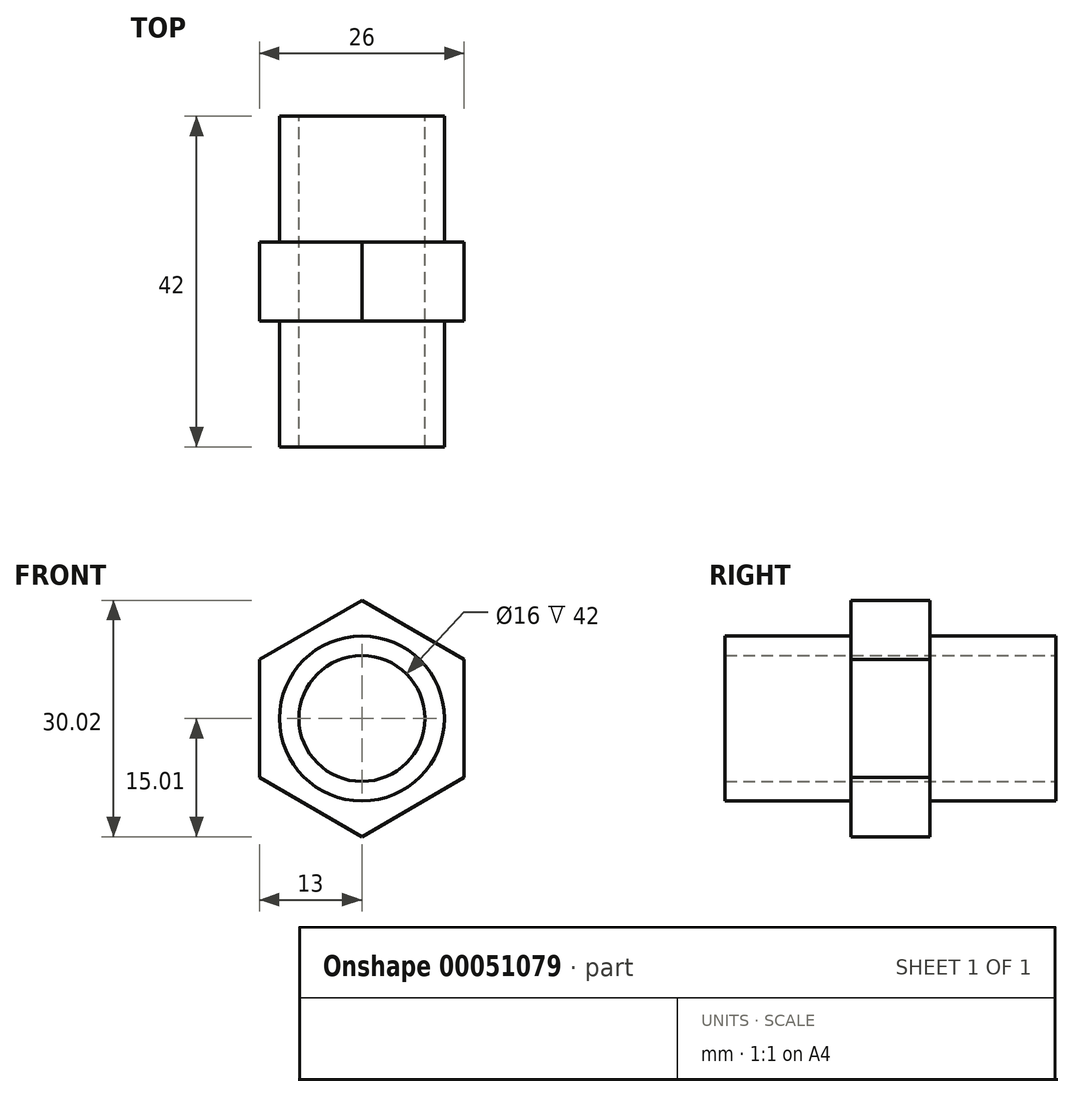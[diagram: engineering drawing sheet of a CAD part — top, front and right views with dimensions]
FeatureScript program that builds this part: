
annotation { "Feature Type Name" : "Feature", "Feature Type Description" : "" }
export const myFeature = defineFeature(function(context is Context, id is Id, definition is map)
    precondition{}
    {
        {
            var Q0;
            Q0=qCreatedBy(makeId("Front.planeOp"),FACE);
            var sketch = newSketch(context, id + "F0", { "sketchPlane" : qUnion([Q0])});
            skCircle(sketch, "E0", {"center": v(0, 0) * mm, "radius": 10.48 * mm});
            skCircle(sketch, "E1", {"center": v(0, 0) * mm, "radius": 8 * mm});
            skSolve(sketch);
        }
        {
            var Q0;
            Q0=qSketchRegion(id+"F0",true);
            extrude(context, id + "F1", {"entities" : qUnion([Q0]), "depth" : 16 * mm});
        }
        {
            var Q0;
            Q0=qCreatedBy(makeId("Front.planeOp"),FACE);
            var sketch = newSketch(context, id + "F2", { "sketchPlane" : qUnion([Q0])});
            skCircle(sketch, "E2", {"center": v(0, 0) * mm, "radius": 8 * mm});
            skCircle(sketch, "E3.cCircle", {"center": v(0, 0) * mm, "radius": 13 * mm, "construction": true});
            skLineSegment(sketch, "E3.0", {"start": v(-13, -7.5) * mm, "end": v(-13, 7.5) * mm});
            skLineSegment(sketch, "E3.1", {"start": v(-13, 7.5) * mm, "end": v(0, 15.01) * mm});
            skLineSegment(sketch, "E3.2", {"start": v(0, 15.01) * mm, "end": v(13, 7.5) * mm});
            skLineSegment(sketch, "E3.3", {"start": v(13, 7.5) * mm, "end": v(13, -7.5) * mm});
            skLineSegment(sketch, "E3.4", {"start": v(13, -7.5) * mm, "end": v(0, -15.01) * mm});
            skLineSegment(sketch, "E3.5", {"start": v(0, -15.01) * mm, "end": v(-13, -7.5) * mm});
            skPoint(sketch, "E3.0.midPoint", {"position": v(-13, 0) * mm});
            skSolve(sketch);
        }
        {
            var Q0;
            Q0=qSketchRegion(id+"F2",true);
            extrude(context, id + "F3", {"entities" : qUnion([Q0]), "operationType" : NewBodyOperationType.ADD, "oppositeDirection" : true, "depth" : 10 * mm});
        }
        {
            var Q0;
            Q0=makeQuery(id+"F3.opExtrude","CAP_FACE",FACE,{"disambiguationData":[OSD([sQuery(id+"F2.wireOp",EDGE,"E2"),sQuery(id+"F2.wireOp",EDGE,"E3.0"),sQuery(id+"F2.wireOp",EDGE,"E3.1"),sQuery(id+"F2.wireOp",EDGE,"E3.2"),sQuery(id+"F2.wireOp",EDGE,"E3.3"),sQuery(id+"F2.wireOp",EDGE,"E3.4"),sQuery(id+"F2.wireOp",EDGE,"E3.5")])],"isStart":false});
            var sketch = newSketch(context, id + "F4", { "sketchPlane" : qUnion([Q0])});
            skCircle(sketch, "E4", {"center": v(0, 0) * mm, "radius": 8 * mm});
            skCircle(sketch, "E5", {"center": v(0, 0) * mm, "radius": 10.48 * mm});
            skSolve(sketch);
        }
        {
            var Q0;
            Q0=qSketchRegion(id+"F4",true);
            extrude(context, id + "F5", {"entities" : qUnion([Q0]), "operationType" : NewBodyOperationType.ADD, "depth" : 16 * mm});
        }
    });
